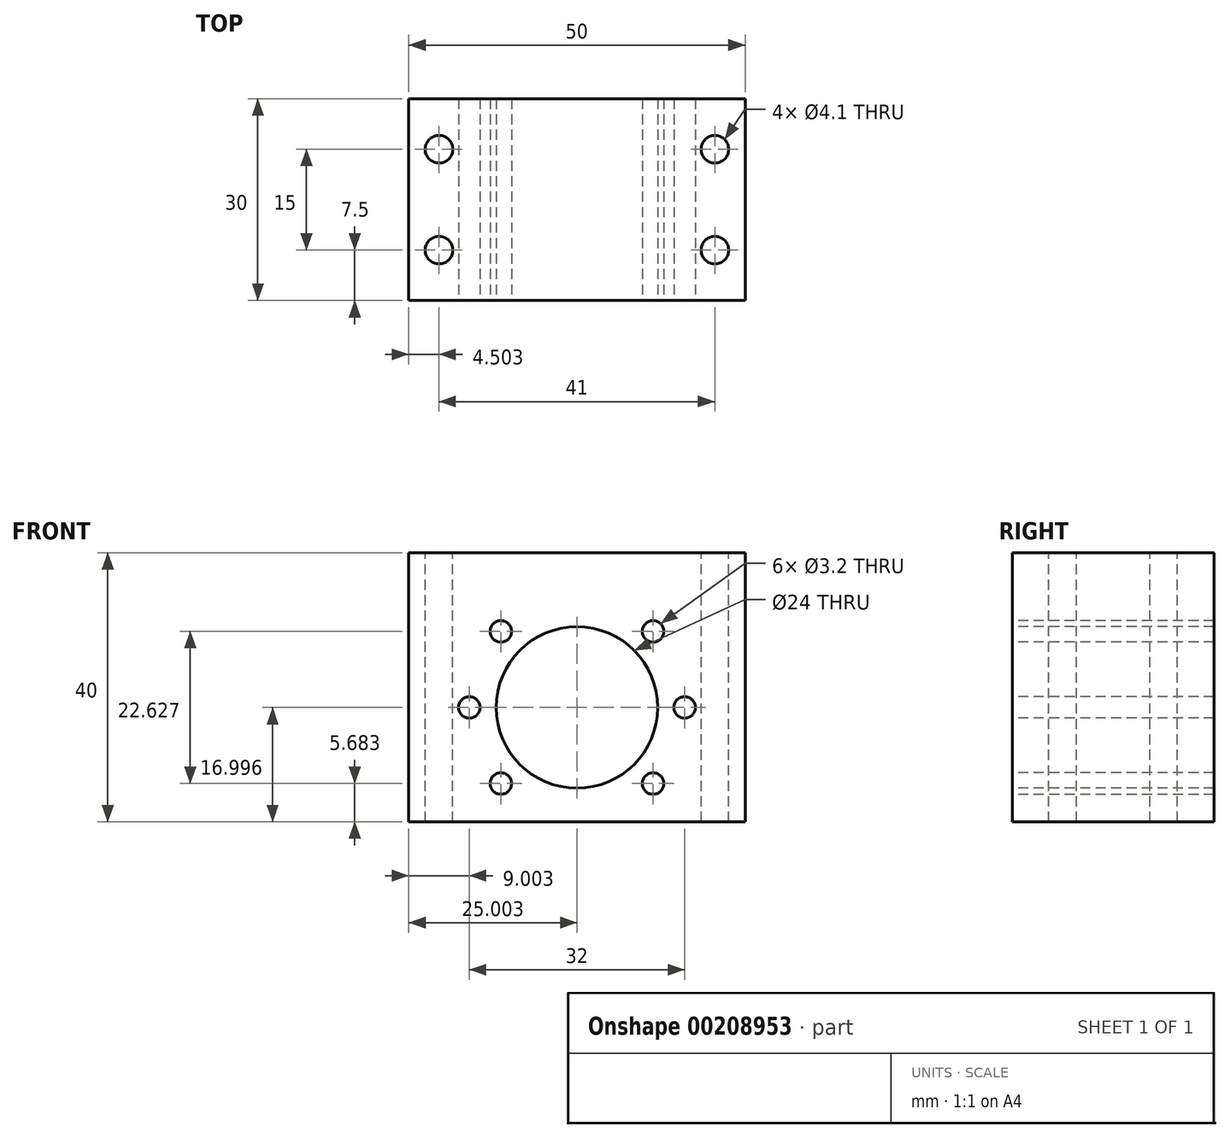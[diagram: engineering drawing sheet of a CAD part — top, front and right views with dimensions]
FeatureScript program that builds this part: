
annotation { "Feature Type Name" : "Feature", "Feature Type Description" : "" }
export const myFeature = defineFeature(function(context is Context, id is Id, definition is map)
    precondition{}
    {
        {
            var Q0;
            Q0=qCreatedBy(makeId("Front.planeOp"),FACE);
            var sketch = newSketch(context, id + "F0", { "sketchPlane" : qUnion([Q0])});
            skLineSegment(sketch, "E0.bottom", {"start": v(-21.59, 18.6) * mm, "end": v(28.41, 18.6) * mm});
            skLineSegment(sketch, "E0.top", {"start": v(-21.59, -21.4) * mm, "end": v(28.41, -21.4) * mm});
            skLineSegment(sketch, "E0.left", {"start": v(-21.59, 18.6) * mm, "end": v(-21.59, -21.4) * mm});
            skLineSegment(sketch, "E0.right", {"start": v(28.41, 18.6) * mm, "end": v(28.41, -21.4) * mm});
            skSolve(sketch);
        }
        {
            var Q0;
            Q0=makeQuery(id+"F0.imprint","IMPRINT",FACE,{"disambiguationData":[TD([[makeQuery(id+"F0.imprint","IMPRINT",EDGE,{"derivedFrom":sQuery(id+"F0.wireOp",EDGE,"E0.bottom")}),-1.0]])]});
            var Q1;
            Q1=qSketchRegion(id+"F2",true);
            extrude(context, id + "F1", {"entities" : qUnion([Q0, Q1]), "depth" : 30 * mm});
        }
        {
            var Q0;
            Q0=makeQuery(id+"F1.opExtrude","CAP_FACE",FACE,{"disambiguationData":[OSD([sQuery(id+"F0.wireOp",EDGE,"E0.bottom"),sQuery(id+"F0.wireOp",EDGE,"E0.top"),sQuery(id+"F0.wireOp",EDGE,"E0.left"),sQuery(id+"F0.wireOp",EDGE,"E0.right")])],"isStart":false});
            var sketch = newSketch(context, id + "F2", { "sketchPlane" : qUnion([Q0])});
            skLineSegment(sketch, "E1", {"start": v(3.41, 18.6) * mm, "end": v(3.41, -21.4) * mm, "construction": true});
            skLineSegment(sketch, "E2", {"start": v(-21.59, -4.4) * mm, "end": v(28.41, -4.4) * mm, "construction": true});
            skCircle(sketch, "E3", {"center": v(3.41, -4.4) * mm, "radius": 20 * mm, "construction": true});
            skCircle(sketch, "E4", {"center": v(3.41, -4.4) * mm, "radius": 12 * mm});
            skLineSegment(sketch, "E5", {"start": v(3.41, -4.4) * mm, "end": v(-25.2, 24.22) * mm, "construction": true});
            skCircle(sketch, "E6", {"center": v(3.41, -4.4) * mm, "radius": 16 * mm, "construction": true});
            skPoint(sketch, "E7", {"position": v(-7.9, 6.92) * mm});
            skPoint(sketch, "E8.MirrorP", {"position": v(14.73, 6.92) * mm});
            skPoint(sketch, "E9.MirrorP", {"position": v(-7.9, -15.7) * mm});
            skPoint(sketch, "E10.MirrorP", {"position": v(14.73, -15.7) * mm});
            skPoint(sketch, "E11", {"position": v(-12.59, -4.4) * mm});
            skPoint(sketch, "E12", {"position": v(19.41, -4.4) * mm});
            skSolve(sketch);
        }
        {
            var Q0;
            Q0=makeQuery(id+"F2.imprint","IMPRINT",FACE,{"disambiguationData":[TD([[makeQuery(id+"F2.imprint","IMPRINT",EDGE,{"derivedFrom":sQuery(id+"F2.wireOp",EDGE,"E4")}),1.0]])]});
            extrude(context, id + "F3", {"entities" : qUnion([Q0]), "operationType" : NewBodyOperationType.REMOVE, "endBound" : BoundingType.THROUGH_ALL, "oppositeDirection" : true, "depth" : 25 * mm});
        }
        {
            var Q0;
            Q0=sQuery(id+"F2.wireOp",VERTEX,"E7");
            var Q1;
            Q1=sQuery(id+"F2.wireOp",VERTEX,"E11");
            var Q2;
            Q2=sQuery(id+"F2.wireOp",VERTEX,"E9.MirrorP");
            var Q3;
            Q3=sQuery(id+"F2.wireOp",VERTEX,"E10.MirrorP");
            var Q4;
            Q4=sQuery(id+"F2.wireOp",VERTEX,"E12");
            var Q5;
            Q5=sQuery(id+"F2.wireOp",VERTEX,"E8.MirrorP");
            var Q6;
            Q6=makeQuery(id+"F1.opExtrude","SWEPT_BODY",BODY,{"disambiguationData":[OSD([sQuery(id+"F0.wireOp",EDGE,"E0.bottom"),sQuery(id+"F0.wireOp",EDGE,"E0.top"),sQuery(id+"F0.wireOp",EDGE,"E0.left"),sQuery(id+"F0.wireOp",EDGE,"E0.right")])]});
            hole(context, id + "F4", {"style" : HoleStyle.SIMPLE, "endStyle" : HoleEndStyle.THROUGH, "standardTappedOrClearance" : lookupTablePath({ "standard" : "ISO", "engagement" : "75%", "pitch" : "0.75 mm", "size" : "M4", "type" : "Tapped" }), "standardBlindInLast" : lookupTablePath({ "standard" : "ISO", "engagement" : "75%", "pitch" : "0.75 mm", "size" : "M4", "type" : "Tapped" }), "holeDiameter" : 3.2 * mm, "locations" : qUnion([Q0, Q1, Q2, Q3, Q4, Q5]), "scope" : qUnion([Q6]), "isTappedThrough" : true, "showTappedDepth" : true});
        }
        {
            var Q0;
            Q0=makeQuery(id+"F1.opExtrude","SWEPT_FACE",FACE,{"disambiguationData":[OSD([sQuery(id+"F0.wireOp",EDGE,"E0.bottom")])]});
            var sketch = newSketch(context, id + "F5", { "sketchPlane" : qUnion([Q0])});
            skLineSegment(sketch, "E13", {"start": v(28.41, -15) * mm, "end": v(-21.59, -15) * mm, "construction": true});
            skLineSegment(sketch, "E14", {"start": v(23.91, -30) * mm, "end": v(23.91, 0) * mm, "construction": true});
            skLineSegment(sketch, "E15", {"start": v(3.41, -30) * mm, "end": v(3.41, 0) * mm, "construction": true});
            skLineSegment(sketch, "E16.MirrorCS", {"start": v(-17.09, -30) * mm, "end": v(-17.09, 0) * mm, "construction": true});
            skLineSegment(sketch, "E17", {"start": v(28.41, -22.5) * mm, "end": v(-21.59, -22.5) * mm, "construction": true});
            skLineSegment(sketch, "E18.MirrorCS", {"start": v(28.41, -7.5) * mm, "end": v(-21.59, -7.5) * mm, "construction": true});
            skPoint(sketch, "E19", {"position": v(23.91, -22.5) * mm});
            skPoint(sketch, "E20", {"position": v(23.91, -7.5) * mm});
            skPoint(sketch, "E21", {"position": v(-17.09, -7.5) * mm});
            skPoint(sketch, "E22", {"position": v(-17.09, -22.5) * mm});
            skSolve(sketch);
        }
        {
            var Q0;
            Q0=sQuery(id+"F5.wireOp",VERTEX,"E19");
            var Q1;
            Q1=sQuery(id+"F5.wireOp",VERTEX,"E20");
            var Q2;
            Q2=sQuery(id+"F5.wireOp",VERTEX,"E21");
            var Q3;
            Q3=sQuery(id+"F5.wireOp",VERTEX,"E22");
            var Q4;
            Q4=makeQuery(id+"F1.opExtrude","SWEPT_BODY",BODY,{"disambiguationData":[OSD([sQuery(id+"F0.wireOp",EDGE,"E0.bottom"),sQuery(id+"F0.wireOp",EDGE,"E0.top"),sQuery(id+"F0.wireOp",EDGE,"E0.left"),sQuery(id+"F0.wireOp",EDGE,"E0.right")])]});
            hole(context, id + "F6", {"style" : HoleStyle.SIMPLE, "endStyle" : HoleEndStyle.THROUGH, "standardTappedOrClearance" : lookupTablePath({ "standard" : "ISO", "engagement" : "75%", "pitch" : "0.9 mm", "size" : "M5", "type" : "Tapped" }), "standardBlindInLast" : lookupTablePath({ "standard" : "ISO", "engagement" : "75%", "pitch" : "0.9 mm", "size" : "M5", "type" : "Tapped" }), "holeDiameter" : 4.1 * mm, "locations" : qUnion([Q0, Q1, Q2, Q3]), "scope" : qUnion([Q4]), "isTappedThrough" : true, "showTappedDepth" : true});
        }
    });
